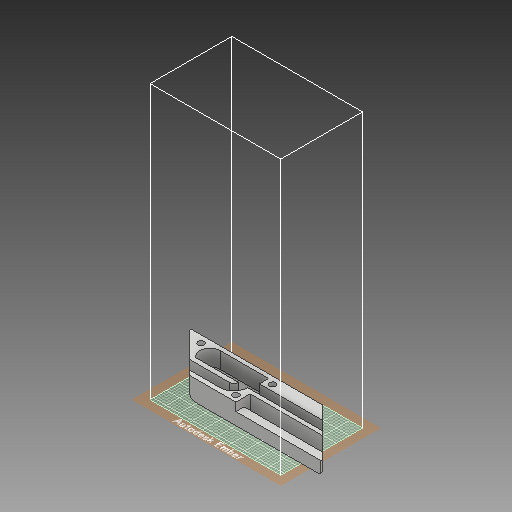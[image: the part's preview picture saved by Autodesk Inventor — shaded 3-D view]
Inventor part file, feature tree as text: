
AUTODESK INVENTOR PART (.ipt)
format: ipt  version: 2018 (Build 220112000, 112)  size: 380,416 bytes
history: native  units: mm
features: sketch x8, extrude x6, other x2, fillet x2, projected_geometry x2, shell x1, sweep x1, chamfer x1
ambient origin geometry x8: Origin, YZ Plane, XZ Plane, XY Plane, X Axis, Y Axis, Z Axis, Center Point
bodies: Body1 (feature_tree)
feature tree (23):
  other  "ソリッド1"
  extrude  "押し出し1"  TaperAngle=45.0deg  [1 undecoded]
  extrude  "押し出し3"  Depth=20.0mm
  extrude  "押し出し4"  Depth=65.0mm
  shell  "シェル1"  Thickness=20.0mm
  fillet  "フィレット2"  Radius=15.2mm
  sketch  "スケッチ7"
  extrude  "押し出し6"  Depth=2.6mm
  other  "作業平面1"
  sweep  "スイープ1"
  extrude  "押し出し7"  Depth=3.75mm
  extrude  "押し出し8"  Depth=3.75mm
  chamfer  "面取り1"  Distance=35.0mm
  fillet  "フィレット4"  Radius=10.0mm
  sketch  "スケッチ1"
  sketch  "スケッチ3"
  sketch  "スケッチ4"
  sketch  "スケッチ6"
  projected_geometry  "投影ループ1"
  sketch  "スケッチ8"
  sketch  "スケッチ9"
  sketch  "スケッチ10"
  projected_geometry  "投影ループ2"
note: 1 required parameter value undecoded (feature->parameter linkage not recoverable at this tier; creation-order binding heuristic only, values carry confidence <= 0.55)
